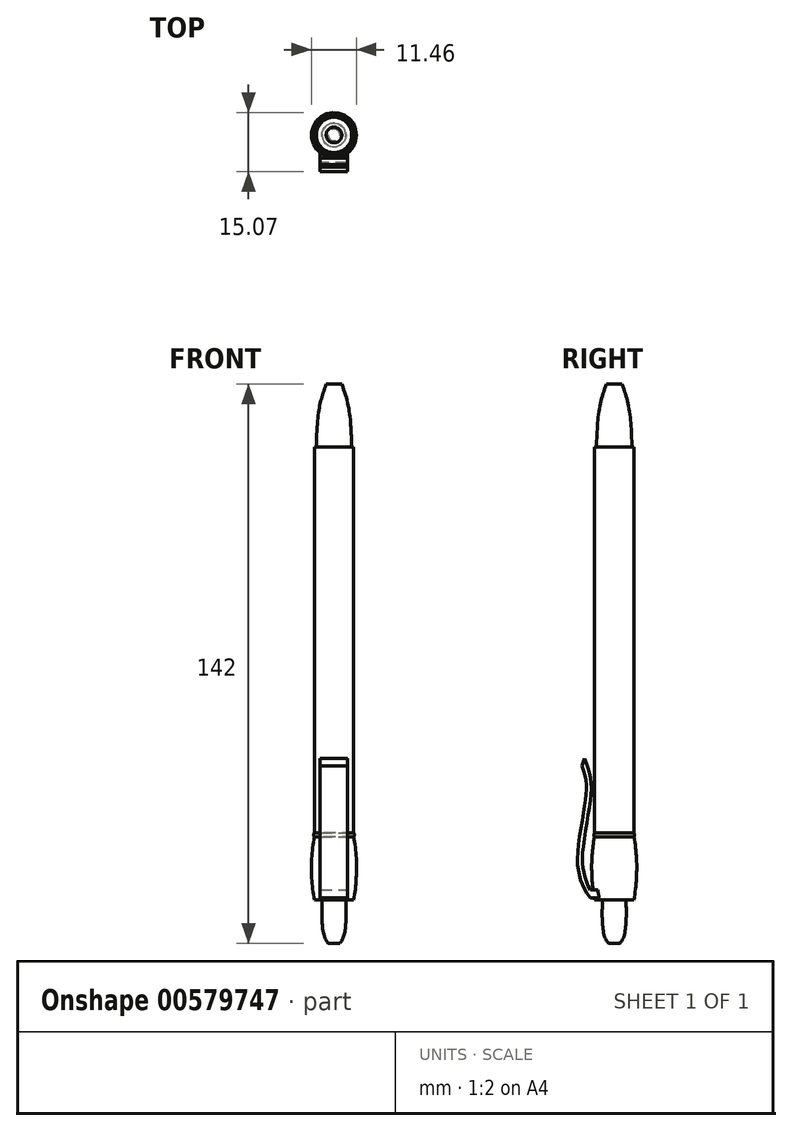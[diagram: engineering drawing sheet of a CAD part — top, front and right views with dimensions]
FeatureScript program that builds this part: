
annotation { "Feature Type Name" : "Feature", "Feature Type Description" : "" }
export const myFeature = defineFeature(function(context is Context, id is Id, definition is map)
    precondition{}
    {
        {
            var Q0;
            Q0=qCreatedBy(makeId("Front.planeOp"),FACE);
            var sketch = newSketch(context, id + "F0", { "sketchPlane" : qUnion([Q0])});
            skLineSegment(sketch, "E0", {"start": v(0, 0) * mm, "end": v(4.5, 0) * mm});
            skLineSegment(sketch, "E1", {"start": v(0, 0) * mm, "end": v(0, 16) * mm});
            skLineSegment(sketch, "E2", {"start": v(0, 16) * mm, "end": v(2, 16) * mm});
            skFitSpline(sketch, "E3", {"points": [v(4.5, 0) * mm, v(2, 16) * mm], "startDerivative": vector(-0.61, 27.03) * mm, "endDerivative": vector(-4.87, 13.4) * mm});
            skSolve(sketch);
        }
        {
            var Q0;
            Q0=makeQuery(id+"F0.imprint","IMPRINT",FACE,{"disambiguationData":[TD([[makeQuery(id+"F0.imprint","IMPRINT",EDGE,{"derivedFrom":sQuery(id+"F0.wireOp",EDGE,"E0")}),1.0]])]});
            var Q1;
            Q1=sQuery(id+"F0.wireOp",EDGE,"E1");
            revolve(context, id + "F1", {"entities" : qUnion([Q0]), "axis" : qUnion([Q1]), "revolveType" : RevolveType.FULL});
        }
        {
            var Q0;
            Q0=qCreatedBy(makeId("Top.planeOp"),FACE);
            var sketch = newSketch(context, id + "F2", { "sketchPlane" : qUnion([Q0])});
            skCircle(sketch, "E4", {"center": v(0, 0) * mm, "radius": 5 * mm});
            skSolve(sketch);
        }
        {
            var Q0;
            Q0 = qSketchRegion(id + "F2", true);
            extrude(context, id + "F3", {"entities" : qUnion([Q0]), "operationType" : NewBodyOperationType.ADD, "oppositeDirection" : true, "depth" : 98 * mm, "offsetDistance" : 25 * mm});
        }
        {
            var Q0;
            Q0=qCreatedBy(makeId("Front.planeOp"),FACE);
            var sketch = newSketch(context, id + "F4", { "sketchPlane" : qUnion([Q0])});
            skLineSegment(sketch, "E5", {"start": v(0, 0) * mm, "end": v(0, -98) * mm});
            skLineSegment(sketch, "E6", {"start": v(0, -99) * mm, "end": v(0, -98) * mm});
            skLineSegment(sketch, "E7", {"start": v(0, -98) * mm, "end": v(5, -98) * mm});
            skLineSegment(sketch, "E8", {"start": v(0, -99) * mm, "end": v(5, -99) * mm});
            skFitSpline(sketch, "E9", {"points": [v(5, -98) * mm, v(5, -99) * mm], "startDerivative": vector(0.62, -0.56) * mm, "endDerivative": vector(-0.62, -0.51) * mm});
            skLineSegment(sketch, "E10", {"start": v(5, -98) * mm, "end": v(5.1, -98) * mm});
            skSolve(sketch);
        }
        {
            var Q0;
            Q0=makeQuery(id+"F4.imprint","IMPRINT",FACE,{"disambiguationData":[TD([[makeQuery(id+"F4.imprint","IMPRINT",EDGE,{"derivedFrom":sQuery(id+"F4.wireOp",EDGE,"E6")}),-1.0]])]});
            var Q1;
            Q1=sQuery(id+"F4.wireOp",EDGE,"E6");
            revolve(context, id + "F5", {"operationType" : NewBodyOperationType.ADD, "entities" : qUnion([Q0]), "axis" : qUnion([Q1]), "revolveType" : RevolveType.FULL});
        }
        {
            var Q0;
            Q0=qCreatedBy(makeId("Front.planeOp"),FACE);
            var sketch = newSketch(context, id + "F6", { "sketchPlane" : qUnion([Q0])});
            skLineSegment(sketch, "E11", {"start": v(0, 0) * mm, "end": v(0, -99) * mm});
            skLineSegment(sketch, "E12", {"start": v(0, -99) * mm, "end": v(0, -115) * mm});
            skLineSegment(sketch, "E13", {"start": v(0, -99) * mm, "end": v(5, -99) * mm});
            skLineSegment(sketch, "E14", {"start": v(0, -115) * mm, "end": v(5, -115) * mm});
            skFitSpline(sketch, "E15", {"points": [v(5, -99) * mm, v(5, -115) * mm], "startDerivative": vector(3.02, -14.6) * mm, "endDerivative": vector(-2.8, -15.06) * mm});
            skSolve(sketch);
        }
        {
            var Q0;
            Q0=makeQuery(id+"F6.imprint","IMPRINT",FACE,{"disambiguationData":[TD([[makeQuery(id+"F6.imprint","IMPRINT",EDGE,{"derivedFrom":sQuery(id+"F6.wireOp",EDGE,"E12")}),1.0]])]});
            var Q1;
            Q1=sQuery(id+"F6.wireOp",EDGE,"E12");
            revolve(context, id + "F7", {"operationType" : NewBodyOperationType.ADD, "entities" : qUnion([Q0]), "axis" : qUnion([Q1]), "revolveType" : RevolveType.FULL});
        }
        {
            var Q0;
            Q0=qCreatedBy(makeId("Front.planeOp"),FACE);
            var sketch = newSketch(context, id + "F8", { "sketchPlane" : qUnion([Q0])});
            skLineSegment(sketch, "E16", {"start": v(0, 0) * mm, "end": v(0, -115) * mm});
            skLineSegment(sketch, "E17", {"start": v(0, -115) * mm, "end": v(0, -126) * mm});
            skLineSegment(sketch, "E18", {"start": v(0, -115) * mm, "end": v(3, -115) * mm});
            skLineSegment(sketch, "E19", {"start": v(0, -126) * mm, "end": v(1.5, -126) * mm});
            skFitSpline(sketch, "E20", {"points": [v(3, -115) * mm, v(1.5, -126) * mm], "startDerivative": vector(0.5, -17.28) * mm, "endDerivative": vector(-4.73, -5.2) * mm});
            skSolve(sketch);
        }
        {
            var Q0;
            Q0=makeQuery(id+"F8.imprint","IMPRINT",FACE,{"disambiguationData":[TD([[makeQuery(id+"F8.imprint","IMPRINT",EDGE,{"derivedFrom":sQuery(id+"F8.wireOp",EDGE,"E17")}),1.0]])]});
            var Q1;
            Q1=sQuery(id+"F8.wireOp",EDGE,"E17");
            revolve(context, id + "F9", {"operationType" : NewBodyOperationType.ADD, "entities" : qUnion([Q0]), "axis" : qUnion([Q1]), "revolveType" : RevolveType.FULL});
        }
        {
            var Q0;
            Q0=qCreatedBy(makeId("Front.planeOp"),FACE);
            var sketch = newSketch(context, id + "F10", { "sketchPlane" : qUnion([Q0])});
            skLineSegment(sketch, "E21", {"start": v(0, -114.47) * mm, "end": v(2.5, -114.47) * mm});
            skLineSegment(sketch, "E22", {"start": v(2.5, -114.47) * mm, "end": v(-2.5, -114.47) * mm});
            skLineSegment(sketch, "E23", {"start": v(-2.5, -114.47) * mm, "end": v(-3.51, -114.47) * mm});
            skLineSegment(sketch, "E24", {"start": v(-3.51, -114.47) * mm, "end": v(3.49, -114.47) * mm});
            skLineSegment(sketch, "E25.bottom", {"start": v(-3.51, -114.47) * mm, "end": v(3.39, -114.47) * mm});
            skLineSegment(sketch, "E25.top", {"start": v(-3.51, -112.47) * mm, "end": v(3.39, -112.47) * mm});
            skLineSegment(sketch, "E25.left", {"start": v(-3.51, -114.47) * mm, "end": v(-3.51, -112.47) * mm});
            skLineSegment(sketch, "E25.right", {"start": v(3.39, -114.47) * mm, "end": v(3.39, -112.47) * mm});
            skSolve(sketch);
        }
        {
            var Q0;
            Q0 = qSketchRegion(id + "F10", true);
            extrude(context, id + "F11", {"entities" : qUnion([Q0]), "operationType" : NewBodyOperationType.ADD, "depth" : 6 * mm, "offsetDistance" : 25 * mm});
        }
        {
            var Q0;
            Q0=qCreatedBy(makeId("Right.planeOp"),FACE);
            var sketch = newSketch(context, id + "F12", { "sketchPlane" : qUnion([Q0])});
            skFitSpline(sketch, "E26", {"points": [v(-6.15, -113.54) * mm, v(-8.28, -108.98) * mm, v(-8.82, -103.27) * mm, v(-7.06, -91.15) * mm, v(-6.73, -84.81) * mm, v(-8, -80.1) * mm], "startDerivative": vector(-19.44, 24.06) * mm, "endDerivative": vector(-9.97, 25.48) * mm});
            skSolve(sketch);
        }
        {
            var Q0;
            Q0=makeQuery(id+"F11.opExtrude","CAP_FACE",FACE,{"disambiguationData":[OSD([sQuery(id+"F10.wireOp",EDGE,"E25.bottom"),sQuery(id+"F10.wireOp",EDGE,"E25.top"),sQuery(id+"F10.wireOp",EDGE,"E25.left"),sQuery(id+"F10.wireOp",EDGE,"E25.right")])],"isStart":false});
            var Q1;
            Q1=sQuery(id+"F12.wireOp",EDGE,"E26");
            sweep(context, id + "F13", {"operationType" : NewBodyOperationType.ADD, "profiles" : qUnion([Q0]), "path" : qUnion([Q1])});
        }
    });
